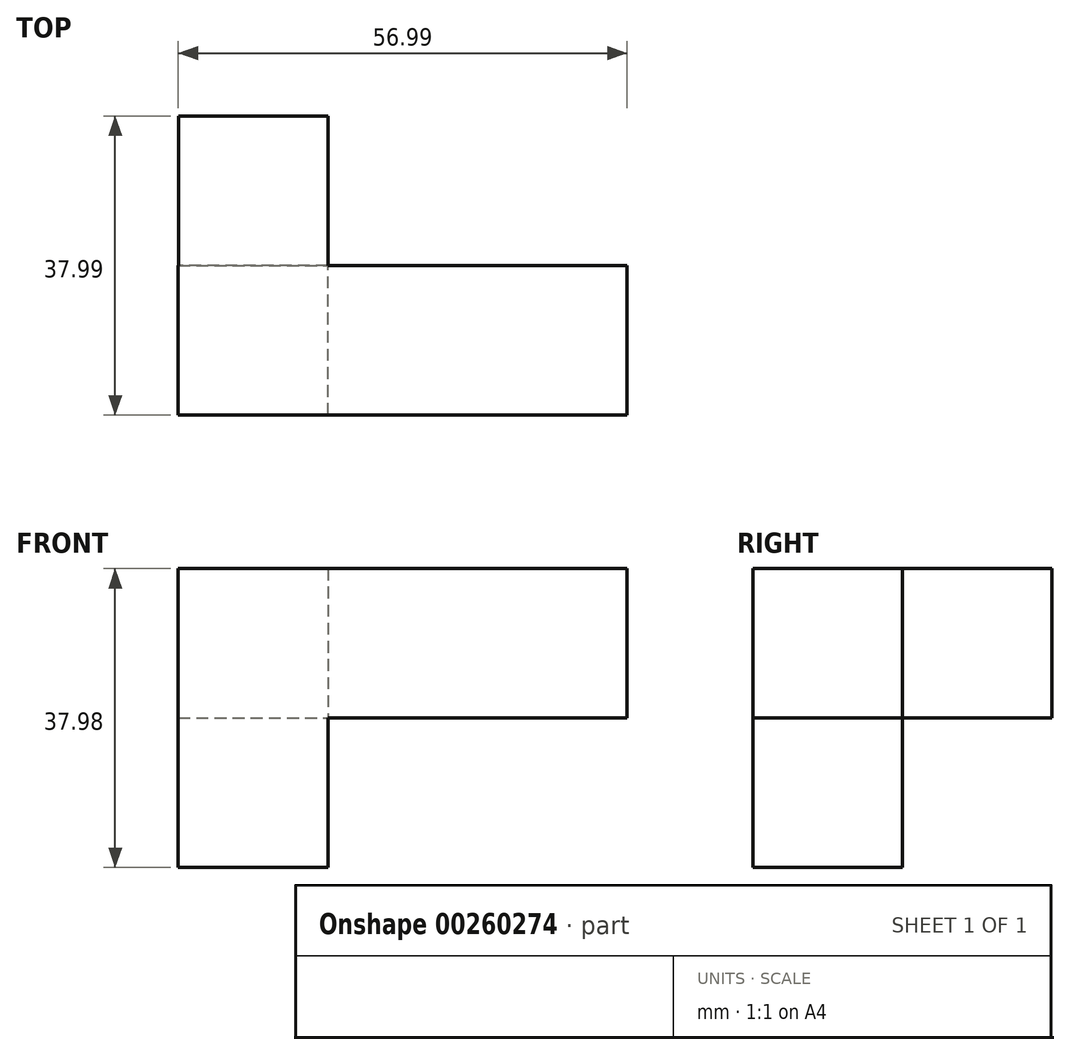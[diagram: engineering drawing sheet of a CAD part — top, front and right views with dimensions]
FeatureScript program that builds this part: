
annotation { "Feature Type Name" : "Feature", "Feature Type Description" : "" }
export const myFeature = defineFeature(function(context is Context, id is Id, definition is map)
    precondition{}
    {
        {
            var Q0;
            Q0=qCreatedBy(makeId("Front.planeOp"),FACE);
            var sketch = newSketch(context, id + "F0", { "sketchPlane" : qUnion([Q0])});
            skLineSegment(sketch, "E0.bottom", {"start": v(19, 18.99) * mm, "end": v(-19, 18.99) * mm});
            skLineSegment(sketch, "E0.top", {"start": v(0, -18.99) * mm, "end": v(-19, -18.99) * mm});
            skLineSegment(sketch, "E0.left", {"start": v(19, 18.99) * mm, "end": v(19, 0) * mm});
            skLineSegment(sketch, "E0.right", {"start": v(-19, 18.99) * mm, "end": v(-19, -18.99) * mm});
            skPoint(sketch, "E0.middle", {"position": v(0, 0) * mm});
            skLineSegment(sketch, "E1", {"start": v(0, 18.99) * mm, "end": v(0, 0) * mm});
            skLineSegment(sketch, "E2", {"start": v(19, 0) * mm, "end": v(0, 0) * mm});
            skLineSegment(sketch, "E3", {"start": v(0, -18.99) * mm, "end": v(0, 0) * mm});
            skLineSegment(sketch, "E4", {"start": v(-19, 0) * mm, "end": v(0, 0) * mm});
            skPoint(sketch, "E5.orphan", {"position": v(19, -18.99) * mm});
            skLineSegment(sketch, "E6.bottom", {"start": v(-19, -18.99) * mm, "end": v(0, -18.99) * mm});
            skLineSegment(sketch, "E6.top", {"start": v(-19, -37.97) * mm, "end": v(0, -37.97) * mm});
            skLineSegment(sketch, "E6.left", {"start": v(-19, -18.99) * mm, "end": v(-19, -37.97) * mm});
            skLineSegment(sketch, "E6.right", {"start": v(0, -18.99) * mm, "end": v(0, -37.97) * mm});
            skLineSegment(sketch, "E7.bottom", {"start": v(19, 18.99) * mm, "end": v(37.99, 18.99) * mm});
            skLineSegment(sketch, "E7.top", {"start": v(19, 0) * mm, "end": v(37.99, 0) * mm});
            skLineSegment(sketch, "E7.right", {"start": v(37.99, 18.99) * mm, "end": v(37.99, 0) * mm});
            skSolve(sketch);
        }
        {
            var Q0;
            {var subQ3=sQuery(id+"F0.wireOp",EDGE,"E1");Q0=makeQuery(id+"F0.imprint","IMPRINT",FACE,{"disambiguationData":[TD([[makeQuery(id+"F0.imprint","IMPRINT",EDGE,{"derivedFrom":subQ3}),-1.0]])]});}
            var Q1;
            Q1=makeQuery(id+"F0.imprint","IMPRINT",FACE,{"disambiguationData":[TD([[makeQuery(id+"F0.imprint","IMPRINT",EDGE,{"derivedFrom":sQuery(id+"F0.wireOp",EDGE,"E6.bottom")}),-1.0]])]});
            var Q2;
            Q2=makeQuery(id+"F0.imprint","IMPRINT",FACE,{"disambiguationData":[TD([[makeQuery(id+"F0.imprint","IMPRINT",EDGE,{"derivedFrom":sQuery(id+"F0.wireOp",EDGE,"E7.bottom")}),-1.0]])]});
            var Q3;
            {var subQ2=sQuery(id+"F0.wireOp",EDGE,"E1");Q3=makeQuery(id+"F0.imprint","IMPRINT",FACE,{"disambiguationData":[TD([[makeQuery(id+"F0.imprint","IMPRINT",EDGE,{"derivedFrom":subQ2}),1.0]])]});}
            var Q4;
            Q4=makeQuery(id+"F0.imprint","IMPRINT",FACE,{"disambiguationData":[TD([[makeQuery(id+"F0.imprint","IMPRINT",EDGE,{"derivedFrom":sQuery(id+"F0.wireOp",EDGE,"E3")}),1.0]])]});
            extrude(context, id + "F1", {"entities" : qUnion([Q0, Q1, Q2, Q3, Q4]), "depth" : 18.99 * mm});
        }
        {
            var Q0;
            Q0=qCreatedBy(makeId("Front.planeOp"),FACE);
            var sketch = newSketch(context, id + "F2", { "sketchPlane" : qUnion([Q0])});
            skLineSegment(sketch, "E8.bottom", {"start": v(-18.99, 18.99) * mm, "end": v(0, 18.99) * mm});
            skLineSegment(sketch, "E8.top", {"start": v(-18.99, 0) * mm, "end": v(0, 0) * mm});
            skLineSegment(sketch, "E8.left", {"start": v(-18.99, 18.99) * mm, "end": v(-18.99, 0) * mm});
            skLineSegment(sketch, "E8.right", {"start": v(0, 18.99) * mm, "end": v(0, 0) * mm});
            skSolve(sketch);
        }
        {
            var Q0;
            Q0 = qSketchRegion(id + "F2", true);
            extrude(context, id + "F3", {"entities" : qUnion([Q0]), "operationType" : NewBodyOperationType.ADD, "oppositeDirection" : true, "depth" : 19 * mm});
        }
    });
